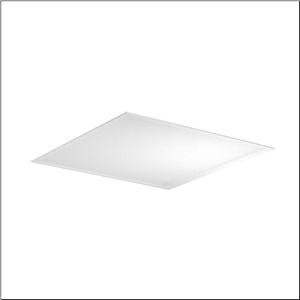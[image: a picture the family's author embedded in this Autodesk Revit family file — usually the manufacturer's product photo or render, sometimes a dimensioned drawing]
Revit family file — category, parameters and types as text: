
# Revit family: apollon_r__31_square_51mp12n72442_260a
name_source: partatom
category: Lighting Fixtures
units: mm (PartAtom-declared; Revit-internal decimal feet)

## family parameters
Cut with Voids When Loaded = No
Host = Face
Light Source = No
Part Type = Normal
Room Calculation Point = No
Round Connector Dimension = Use Diameter
Shared = No

## types (1)
- Apollon® 31 square (1 x LED, 4000 lm, 27.5 W, 4000K)
    Apparent Load = 28 VA
    CIE Flux Codes = 46 78 95 100 100
    Color Rendering = 80
    Color Temperature = 4000K
    Default Elevation = 1800 mm
    Description = Apollon® 31 square, office luminaire, primary optical cover: micro prismatic cover, of PMMA, CAT 2 (L<= 3000cd/m²), light emission: direct distribution, primary light characteristic: symmetric, installation type: lay-in mounting, LED, rated luminous flux: 4.000lm, luminous efficacy: 145lm/W, light colour: 840, colour temperature: 4000K, with terminal, 3-pole, mains connection: 220..240V, AC, 50/60Hz, rated input power: 28W, housing, of aluminium, traffic white (RAL 9016), module: M600, length: 595mm, width: 595mm, height: 32mm, housing upper side, of sheet steel, galvanised, protection rating (complete): IP20, protection rating (on room side): IP40, insulation class (complete): insulation class II (safety insulation), certification: CE, ENEC, impact resistance: IK03, permissible operating ambient temperature: -20..+40°C, permissible storage temperature: -20..+60°C, packaging unit: 1 piece
    Height = 0 mm  [stored 0 ft]
    Lamp = 1 x LED
    Lamp Light Flux = 4000 lm
    Lamp Power = 27.5 W
    Lamp count = 1
    Length = 595 mm
    Luminous efficacy = 145 lm/W
    Manufacturer = Siteco
    ModVariant = No
    Model = 51MP12N72442
    Mounting Place = Ceiling
    Mounting Type = Recessed
    Number of Poles = 1
    OnlyDefault = Yes
    Power Factor = 1
    Product Name = Apollon® 31 square
    Product group = office luminaire | ceiling recessed
    ProductGroupID = 400
    Protection Class = Protection class II
    Protection Degree = IP 20
    RLX_Detail_Level = 1
    RLX_Emergency_Light_Flux = 0 lm
    RLX_Emergency_Type = 0
    RLX_Emergency_Type_DB = No
    RlxData = <blob elided: 12317 chars, md5=6de87240>
    Socket = socket
    Standby Power = 0 W
    System Light Flux = 4000 lm
    System Power = 28 W
    Type Comments = Product without accessories
    Type Image = l_1291035.jpg
    URL = http://relux.com
    VarID = ---
    Voltage = 0 V
    Weight = 0.00 kg
    Width = 595 mm

note: [stored X ft] marks values corroborated as IEEE doubles in the binary element streams (Revit-internal decimal feet)

## geometry (parser evidence)
native form markers: Sweep x9
no freeform markers — native parametric forms only
